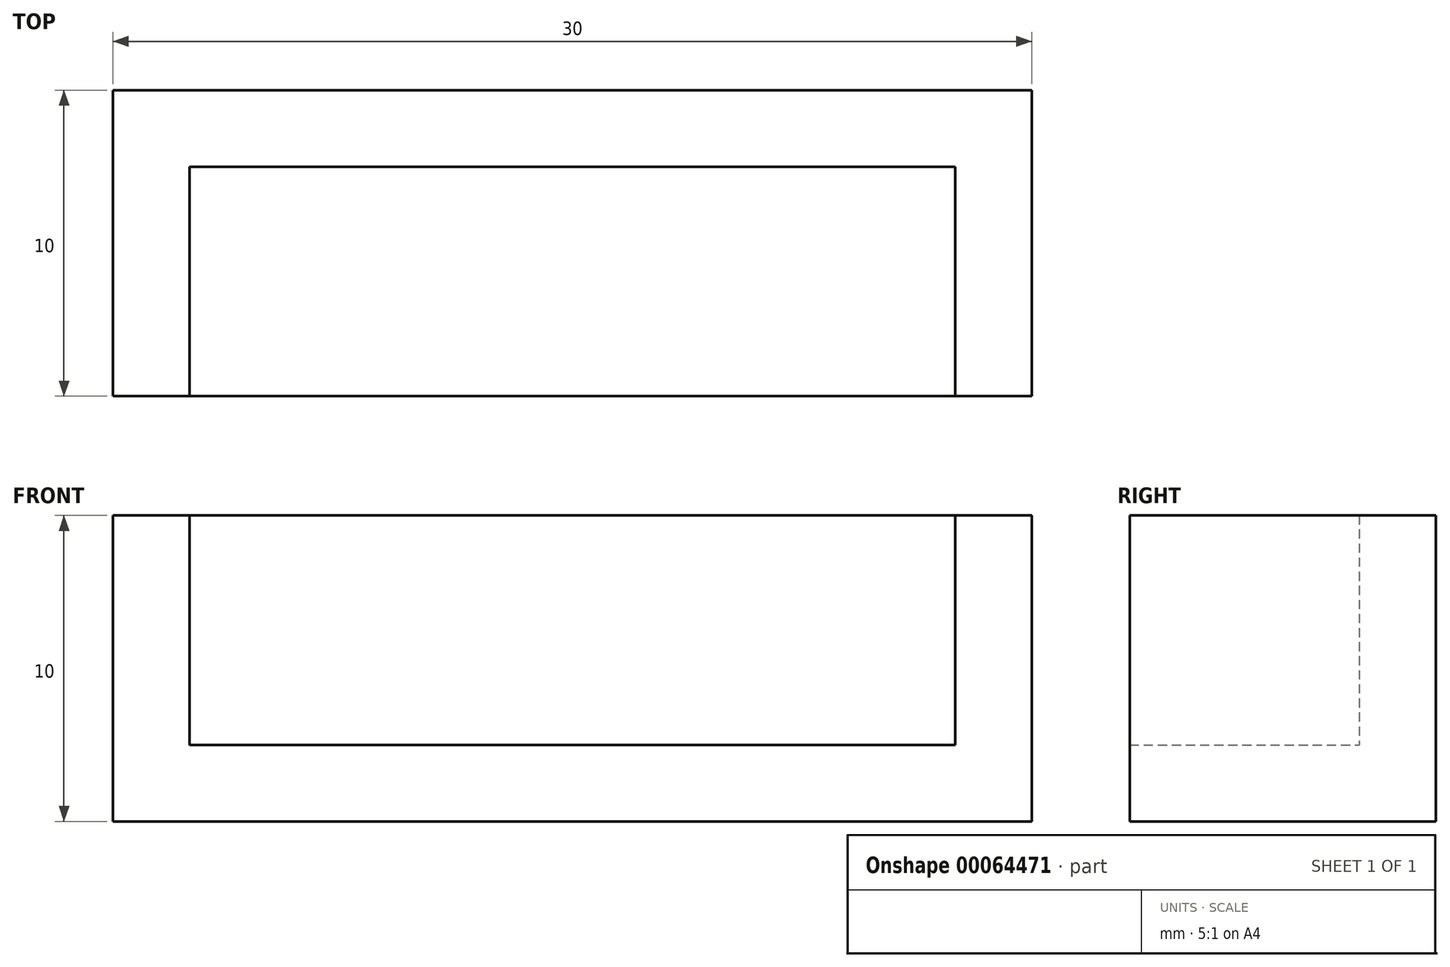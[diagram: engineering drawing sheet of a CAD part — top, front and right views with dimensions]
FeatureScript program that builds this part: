
annotation { "Feature Type Name" : "Feature", "Feature Type Description" : "" }
export const myFeature = defineFeature(function(context is Context, id is Id, definition is map)
    precondition{}
    {
        {
            var Q0;
            Q0=qCreatedBy(makeId("Top.planeOp"),FACE);
            var sketch = newSketch(context, id + "F0", { "sketchPlane" : qUnion([Q0])});
            skLineSegment(sketch, "E0.rect.bottom", {"start": v(15, -5) * mm, "end": v(-15, -5) * mm});
            skLineSegment(sketch, "E0.rect.top", {"start": v(15, 5) * mm, "end": v(-15, 5) * mm});
            skLineSegment(sketch, "E0.rect.left", {"start": v(15, -5) * mm, "end": v(15, 5) * mm});
            skLineSegment(sketch, "E0.rect.right", {"start": v(-15, -5) * mm, "end": v(-15, 5) * mm});
            skPoint(sketch, "E0.rect.middle", {"position": v(0, 0) * mm});
            skSolve(sketch);
        }
        {
            var Q0;
            Q0 = qSketchRegion(id + "F0", true);
            extrude(context, id + "F1", {"entities" : qUnion([Q0]), "depth" : 10 * mm});
        }
        {
            var Q0;
            Q0=makeQuery(id+"F1.opExtrude","CAP_FACE",FACE,{"disambiguationData":[OSD([sQuery(id+"F0.wireOp",EDGE,"E0.rect.bottom"),sQuery(id+"F0.wireOp",EDGE,"E0.rect.top"),sQuery(id+"F0.wireOp",EDGE,"E0.rect.left"),sQuery(id+"F0.wireOp",EDGE,"E0.rect.right")])],"isStart":false});
            var Q1;
            Q1=makeQuery(id+"F1.opExtrude","SWEPT_FACE",FACE,{"disambiguationData":[OSD([sQuery(id+"F0.wireOp",EDGE,"E0.rect.bottom")])]});
            shell(context, id + "F2", {"entities" : qUnion([Q0, Q1]), "thickness" : 2.5 * mm});
        }
    });
